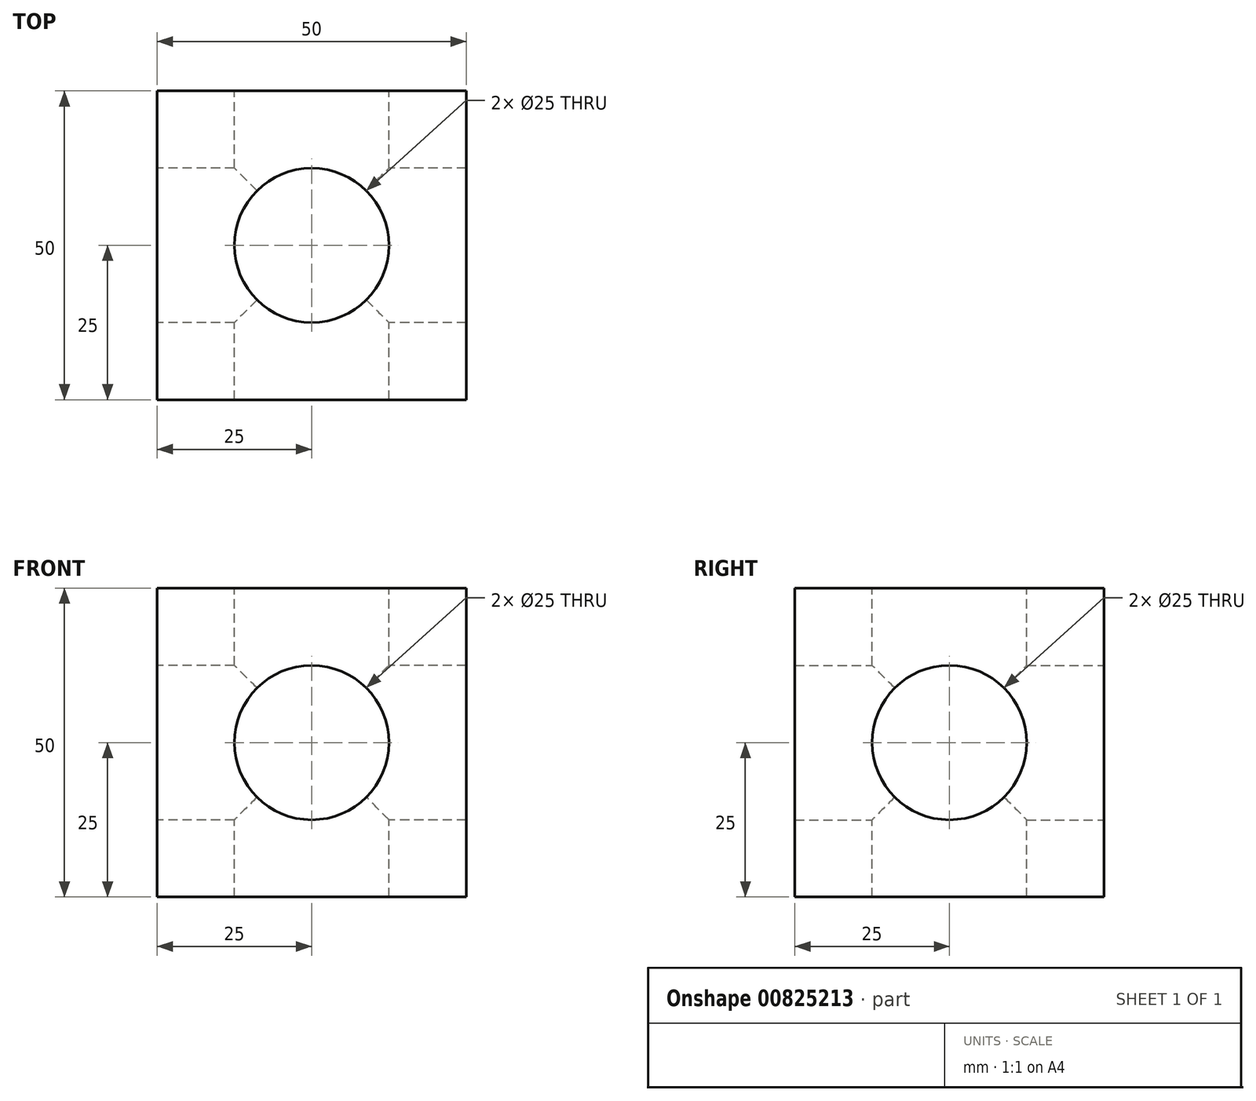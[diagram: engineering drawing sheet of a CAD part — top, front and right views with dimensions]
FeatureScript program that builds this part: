
annotation { "Feature Type Name" : "Feature", "Feature Type Description" : "" }
export const myFeature = defineFeature(function(context is Context, id is Id, definition is map)
    precondition{}
    {
        {
            var Q0;
            Q0=qCreatedBy(makeId("Top.planeOp"),FACE);
            var sketch = newSketch(context, id + "F0", { "sketchPlane" : qUnion([Q0])});
            skLineSegment(sketch, "E0.bottom", {"start": v(25, -25) * mm, "end": v(-25, -25) * mm});
            skLineSegment(sketch, "E0.top", {"start": v(25, 25) * mm, "end": v(-25, 25) * mm});
            skLineSegment(sketch, "E0.left", {"start": v(25, -25) * mm, "end": v(25, 25) * mm});
            skLineSegment(sketch, "E0.right", {"start": v(-25, -25) * mm, "end": v(-25, 25) * mm});
            skPoint(sketch, "E0.middle", {"position": v(0, 0) * mm});
            skSolve(sketch);
        }
        {
            var Q0;
            Q0=makeQuery(id+"F0.imprint","IMPRINT",FACE,{"disambiguationData":[TD([[makeQuery(id+"F0.imprint","IMPRINT",EDGE,{"derivedFrom":sQuery(id+"F0.wireOp",EDGE,"E0.bottom")}),-1.0]])]});
            extrude(context, id + "F1", {"entities" : qUnion([Q0]), "depth" : 50 * mm, "offsetDistance" : 25 * mm});
        }
        {
            var Q0;
            Q0=makeQuery(id+"F1.opExtrude","CAP_FACE",FACE,{"disambiguationData":[OSD([sQuery(id+"F0.wireOp",EDGE,"E0.bottom"),sQuery(id+"F0.wireOp",EDGE,"E0.top"),sQuery(id+"F0.wireOp",EDGE,"E0.left"),sQuery(id+"F0.wireOp",EDGE,"E0.right")])],"isStart":false});
            var sketch = newSketch(context, id + "F2", { "sketchPlane" : qUnion([Q0])});
            skCircle(sketch, "E1", {"center": v(0, 0) * mm, "radius": 12.5 * mm});
            skSolve(sketch);
        }
        {
            var Q0;
            Q0 = qSketchRegion(id + "F2", true);
            extrude(context, id + "F3", {"entities" : qUnion([Q0]), "operationType" : NewBodyOperationType.REMOVE, "oppositeDirection" : true, "depth" : 50 * mm, "offsetDistance" : 25 * mm});
        }
        {
            var Q0;
            Q0=makeQuery(id+"F1.opExtrude","SWEPT_FACE",FACE,{"disambiguationData":[OSD([sQuery(id+"F0.wireOp",EDGE,"E0.right")])]});
            var sketch = newSketch(context, id + "F4", { "sketchPlane" : qUnion([Q0])});
            skCircle(sketch, "E2", {"center": v(0, 25) * mm, "radius": 12.5 * mm});
            skSolve(sketch);
        }
        {
            var Q0;
            Q0=makeQuery(id+"F4.imprint","IMPRINT",FACE,{"disambiguationData":[TD([[makeQuery(id+"F4.imprint","IMPRINT",EDGE,{"derivedFrom":sQuery(id+"F4.wireOp",EDGE,"E2")}),1.0]])]});
            extrude(context, id + "F5", {"entities" : qUnion([Q0]), "operationType" : NewBodyOperationType.REMOVE, "oppositeDirection" : true, "depth" : 50 * mm, "offsetDistance" : 25 * mm});
        }
        {
            var Q0;
            Q0=makeQuery(id+"F1.opExtrude","SWEPT_FACE",FACE,{"disambiguationData":[OSD([sQuery(id+"F0.wireOp",EDGE,"E0.top")])]});
            var sketch = newSketch(context, id + "F6", { "sketchPlane" : qUnion([Q0])});
            skCircle(sketch, "E3", {"center": v(0, 25) * mm, "radius": 12.5 * mm});
            skSolve(sketch);
        }
        {
            var Q0;
            Q0=makeQuery(id+"F6.imprint","IMPRINT",FACE,{"disambiguationData":[TD([[makeQuery(id+"F6.imprint","IMPRINT",EDGE,{"derivedFrom":sQuery(id+"F6.wireOp",EDGE,"E3")}),1.0]])]});
            var Q1;
            Q1=sQuery(id+"F6.wireOp",EDGE,"E3");
            extrude(context, id + "F7", {"entities" : qUnion([Q0]), "operationType" : NewBodyOperationType.REMOVE, "surfaceEntities" : qUnion([Q1]), "oppositeDirection" : true, "depth" : 50 * mm, "offsetDistance" : 25 * mm});
        }
    });
